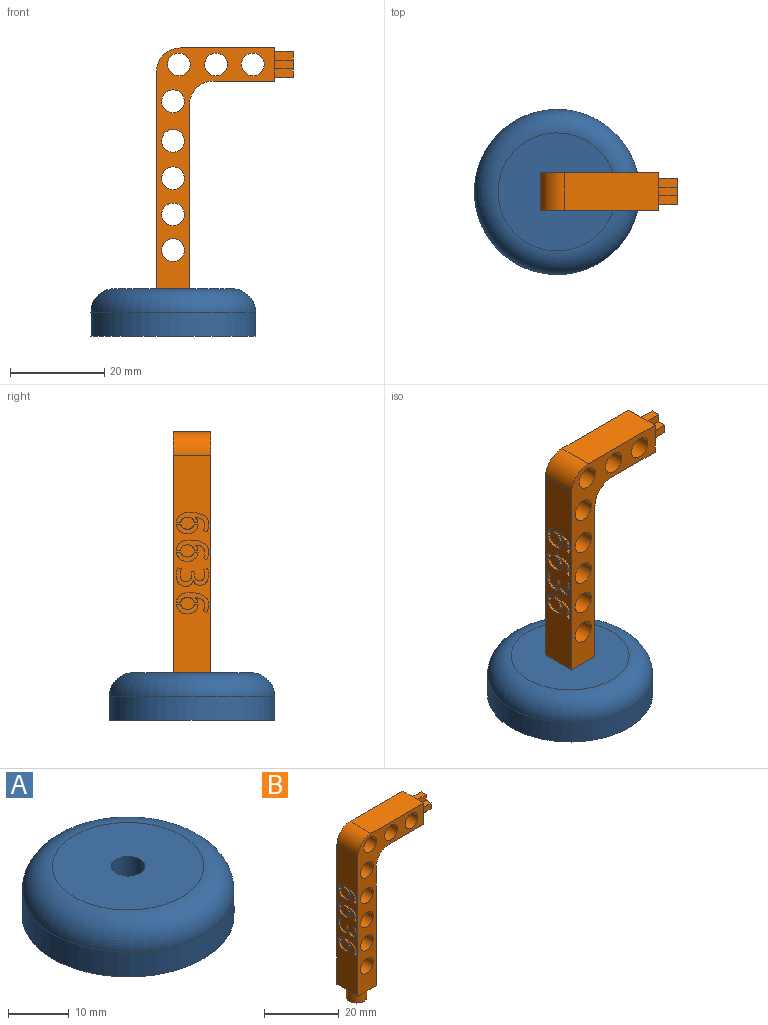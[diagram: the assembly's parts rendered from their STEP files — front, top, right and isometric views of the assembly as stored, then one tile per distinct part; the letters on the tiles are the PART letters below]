
ASSEMBLY  parts=2 mates=1
PART A: 6 faces, bbox 37.9x37.9x10 mm
  f0: cylinder r=17.5mm len=35mm, axis (0,0,-1), area 549.8mm2, adj f2,f3
  f1: plane 25x25mm, normal (0,0,1), area 466.2mm2, adj f3,f4
  f2: plane 35x35mm, normal (0,0,-1), area 962.1mm2, adj f0
  f3: torus R=12.5mm, axis (0,0,1), area 773.9mm2, adj f0,f1
  f4: cylinder r=2.8mm len=5.6mm, axis (0,0,1), area 70.4mm2, adj f1,f5
  f5: plane 5.6x5.6mm, normal (0,0,1), area 24.6mm2, adj f4
PART B: 220 faces, bbox 29x7.9x55 mm
  f0: plane 46x7.9mm, normal (-1,0,0), area 308.5mm2, adj f3,f6,f7,f8,f33,f34,f35,f36
  f1: plane 7.9x7mm, normal (1,0,0), area 38.2mm2, adj f2,f5,f6,f7,f12,f13,f14,f15
  f2: plane 20x7.9mm, normal (0,0,1), area 158mm2, adj f1,f6,f7,f8
  f3: plane 7.9x7mm, normal (0,0,-1), area 31.1mm2, adj f0,f4,f6,f7,f10
  f4: plane 39x7.9mm, normal (1,0,0), area 308.1mm2, adj f3,f6,f7,f9
  f5: plane 13x7.9mm, normal (0,0,-1), area 102.7mm2, adj f1,f6,f7,f9
  f6: plane 51x25mm, normal (0,-1,0), area 337mm2, adj f0,f1,f2,f3,f4,f5,f8,f9
  f7: plane 51x25mm, normal (0,1,0), area 337mm2, adj f0,f1,f2,f3,f4,f5,f8,f9
  f8: cylinder r=5mm len=7.9mm, axis (0,1,0), area 62mm2, adj f0,f2,f6,f7
  f9: cylinder r=5mm len=7.9mm, axis (0,-1,0), area 62mm2, adj f4,f5,f6,f7
  f10: cylinder r=2.77mm len=5.55mm, axis (0,0,1), area 69.7mm2, adj f3,f11
  f11: plane 5.55x5.55mm, normal (0,0,-1), area 24.2mm2, adj f10
  f12: plane 4x1.85mm, normal (0,0,1), area 7.4mm2, adj f1,f13,f23,f24
  f13: plane 4x1.85mm, normal (0,-1,0), area 7.4mm2, adj f1,f12,f14,f24
  f14: plane 4x1.85mm, normal (0,0,1), area 7.4mm2, adj f1,f13,f15,f24
  f15: plane 4x1.85mm, normal (0,-1,0), area 7.4mm2, adj f1,f14,f16,f24
  f16: plane 4x1.85mm, normal (0,0,-1), area 7.4mm2, adj f1,f15,f17,f24
  f17: plane 4x1.85mm, normal (0,-1,0), area 7.4mm2, adj f1,f16,f18,f24
  f18: plane 4x1.85mm, normal (0,0,-1), area 7.4mm2, adj f1,f17,f19,f24
  f19: plane 4x1.85mm, normal (0,1,0), area 7.4mm2, adj f1,f18,f20,f24
  f20: plane 4x1.85mm, normal (0,0,-1), area 7.4mm2, adj f1,f19,f21,f24
  f21: plane 4x1.85mm, normal (0,1,0), area 7.4mm2, adj f1,f20,f22,f24
  f22: plane 4x1.85mm, normal (0,0,1), area 7.4mm2, adj f1,f21,f23,f24
  f23: plane 4x1.85mm, normal (0,1,0), area 7.4mm2, adj f1,f12,f22,f24
  f24: plane 5.55x5.55mm, normal (1,0,0), area 17.1mm2, adj f12,f13,f14,f15,f16,f17,f18,f19
  f25: cylinder r=2.41mm len=7.9mm, axis (0,-1,0), area 119.6mm2, adj f6,f7
  f26: cylinder r=2.41mm len=7.9mm, axis (0,-1,0), area 119.6mm2, adj f6,f7
  f27: cylinder r=2.41mm len=7.9mm, axis (0,-1,0), area 119.6mm2, adj f6,f7
  f28: cylinder r=2.41mm len=7.9mm, axis (0,-1,0), area 119.6mm2, adj f6,f7
  f29: cylinder r=2.41mm len=7.9mm, axis (0,-1,0), area 119.6mm2, adj f6,f7
  f30: cylinder r=2.41mm len=7.9mm, axis (0,-1,0), area 119.6mm2, adj f6,f7
  f31: cylinder r=2.41mm len=7.9mm, axis (0,-1,0), area 119.6mm2, adj f6,f7
  f32: cylinder r=2.41mm len=7.9mm, axis (0,-1,0), area 119.6mm2, adj f6,f7
  f33: extruded ~0.7x0.65mm, area 0.5mm2, adj f0,f34,f63,f64
  f34: extruded ~0.72x0.7mm, area 0.5mm2, adj f0,f33,f35,f64
  f35: extruded ~0.7x0.56mm, area 0.4mm2, adj f0,f34,f36,f64
  f36: plane 0.75x0.7mm, normal (0,-0.42,0.91), area 0.6mm2, adj f0,f35,f37,f64
  f37: extruded ~0.77x0.7mm, area 0.6mm2, adj f0,f36,f38,f64
  f38: extruded ~0.96x0.7mm, area 0.7mm2, adj f0,f37,f39,f64
  f39: extruded ~0.86x0.7mm, area 0.6mm2, adj f0,f38,f40,f64
  f40: extruded ~0.78x0.7mm, area 0.7mm2, adj f0,f39,f41,f64
  f41: extruded ~1.26x0.7mm, area 1mm2, adj f0,f40,f42,f64
  f42: extruded ~2x0.7mm, area 1.4mm2, adj f0,f41,f43,f64
  f43: extruded ~1.05x0.7mm, area 0.7mm2, adj f0,f42,f44,f64
  f44: extruded ~0.84x0.7mm, area 0.7mm2, adj f0,f43,f45,f64
  f45: extruded ~0.7x0.69mm, area 0.6mm2, adj f0,f44,f46,f64
  f46: extruded ~0.97x0.7mm, area 0.7mm2, adj f0,f45,f47,f64
  f47: plane 0.89x0.7mm, normal (0,0,1), area 0.6mm2, adj f0,f46,f48,f64
  f48: extruded ~0.7x0.46mm, area 0.3mm2, adj f0,f47,f49,f64
  f49: extruded ~0.7x0.37mm, area 0.3mm2, adj f0,f48,f50,f64
  f50: extruded ~0.7x0.45mm, area 0.4mm2, adj f0,f49,f51,f64
  f51: extruded ~0.7x0.55mm, area 0.4mm2, adj f0,f50,f52,f64
  f52: extruded ~0.7x0.54mm, area 0.4mm2, adj f0,f51,f53,f64
  f53: extruded ~0.7x0.44mm, area 0.4mm2, adj f0,f52,f54,f64
  f54: extruded ~0.7x0.36mm, area 0.3mm2, adj f0,f53,f55,f64
  f55: extruded ~0.7x0.46mm, area 0.3mm2, adj f0,f54,f56,f64
  f56: plane 0.8x0.7mm, normal (0,0,1), area 0.6mm2, adj f0,f55,f57,f64
  f57: extruded ~0.7x0.66mm, area 0.5mm2, adj f0,f56,f58,f64
  f58: extruded ~0.7x0.38mm, area 0.4mm2, adj f0,f57,f59,f64
  f59: extruded ~0.7x0.04mm, area 0mm2, adj f0,f58,f60,f64
  f60: extruded ~0.7x0.04mm, area 0mm2, adj f0,f59,f61,f64
  f61: extruded ~0.74x0.7mm, area 0.5mm2, adj f0,f60,f62,f64
  f62: extruded ~0.7x0.63mm, area 0.5mm2, adj f0,f61,f63,f64
  f63: extruded ~0.7x0.45mm, area 0.4mm2, adj f0,f33,f62,f64
  f64: plane 6.8x4.15mm, normal (-1,0,0), area 9.7mm2, adj f33,f34,f35,f36,f37,f38,f39,f40
  f65: extruded ~0.7x0.43mm, area 0.3mm2, adj f0,f66,f109,f110
  f66: extruded ~0.7x0.35mm, area 0.3mm2, adj f0,f65,f67,f110
  f67: extruded ~0.7x0.35mm, area 0.3mm2, adj f0,f66,f68,f110
  f68: extruded ~0.7x0.41mm, area 0.3mm2, adj f0,f67,f69,f110
  f69: extruded ~0.7x0.51mm, area 0.4mm2, adj f0,f68,f70,f110
  f70: extruded ~0.84x0.7mm, area 0.6mm2, adj f0,f69,f71,f110
  f71: extruded ~0.7x0.58mm, area 0.5mm2, adj f0,f70,f72,f110
  f72: extruded ~0.7x0.67mm, area 0.5mm2, adj f0,f71,f73,f110
  f73: extruded ~0.81x0.7mm, area 0.6mm2, adj f0,f72,f74,f110
  f74: extruded ~0.93x0.7mm, area 0.7mm2, adj f0,f73,f75,f110
  f75: extruded ~0.7x0.54mm, area 0.4mm2, adj f0,f74,f76,f110
  f76: plane 0.82x0.7mm, normal (0,-0.36,-0.93), area 0.6mm2, adj f0,f75,f77,f110
  f77: extruded ~0.7x0.38mm, area 0.3mm2, adj f0,f76,f78,f110
  f78: extruded ~0.7x0.67mm, area 0.5mm2, adj f0,f77,f79,f110
  f79: extruded ~0.7x0.66mm, area 0.5mm2, adj f0,f78,f80,f110
  f80: extruded ~0.7x0.36mm, area 0.3mm2, adj f0,f79,f81,f110
  f81: extruded ~0.7x0.34mm, area 0.3mm2, adj f0,f80,f82,f110
  f82: extruded ~0.7x0.35mm, area 0.2mm2, adj f0,f81,f83,f110
  f83: extruded ~0.7x0.63mm, area 0.5mm2, adj f0,f82,f84,f110
  f84: extruded ~0.7x0.31mm, area 0.3mm2, adj f0,f83,f85,f110
  f85: extruded ~0.7x0.39mm, area 0.3mm2, adj f0,f84,f86,f110
  f86: extruded ~0.7x0.4mm, area 0.3mm2, adj f0,f85,f87,f110
  f87: plane 0.7x0.62mm, normal (0,1,0), area 0.4mm2, adj f0,f86,f88,f110
  f88: plane 0.74x0.7mm, normal (0,-0.01,-1), area 0.5mm2, adj f0,f87,f89,f110
  f89: plane 0.92x0.7mm, normal (0,-1,0), area 0.6mm2, adj f0,f88,f90,f110
  f90: extruded ~0.83x0.7mm, area 0.6mm2, adj f0,f89,f91,f110
  f91: extruded ~0.83x0.7mm, area 0.6mm2, adj f0,f90,f92,f110
  f92: extruded ~0.86x0.7mm, area 0.7mm2, adj f0,f91,f93,f110
  f93: extruded ~0.94x0.7mm, area 0.7mm2, adj f0,f92,f94,f110
  f94: extruded ~0.7x0.67mm, area 0.5mm2, adj f0,f93,f95,f110
  f95: extruded ~0.7x0.38mm, area 0.3mm2, adj f0,f94,f96,f110
  f96: extruded ~0.7x0.21mm, area 0.2mm2, adj f0,f95,f97,f110
  f97: extruded ~0.7x0.16mm, area 0.1mm2, adj f0,f96,f98,f110
  f98: plane 0.78x0.7mm, normal (0,0.3,-0.95), area 0.6mm2, adj f0,f97,f99,f110
  f99: extruded ~0.7x0.61mm, area 0.5mm2, adj f0,f98,f100,f110
  f100: extruded ~1.2x0.7mm, area 0.8mm2, adj f0,f99,f101,f110
  f101: extruded ~0.7x0.3mm, area 0.2mm2, adj f0,f100,f102,f110
  f102: extruded ~0.7x0.43mm, area 0.3mm2, adj f0,f101,f103,f110
  f103: extruded ~0.7x0.49mm, area 0.4mm2, adj f0,f102,f104,f110
  f104: extruded ~0.7x0.45mm, area 0.4mm2, adj f0,f103,f105,f110
  f105: extruded ~0.7x0.55mm, area 0.5mm2, adj f0,f104,f106,f110
  f106: extruded ~0.79x0.7mm, area 0.6mm2, adj f0,f105,f107,f110
  f107: extruded ~0.7x0.66mm, area 0.5mm2, adj f0,f106,f108,f110
  f108: extruded ~0.7x0.49mm, area 0.4mm2, adj f0,f107,f109,f110
  f109: extruded ~0.7x0.41mm, area 0.4mm2, adj f0,f65,f108,f110
  f110: plane 6.78x3.95mm, normal (-1,0,0), area 11.1mm2, adj f65,f66,f67,f68,f69,f70,f71,f72
  f111: extruded ~0.83x0.7mm, area 0.6mm2, adj f0,f112,f124,f125
  f112: plane 0.83x0.7mm, normal (0,0,-1), area 0.6mm2, adj f0,f111,f113,f125
  f113: extruded ~0.75x0.7mm, area 0.6mm2, adj f0,f112,f114,f125
  f114: extruded ~0.94x0.7mm, area 0.7mm2, adj f0,f113,f115,f125
  f115: extruded ~0.97x0.7mm, area 0.7mm2, adj f0,f114,f116,f125
  f116: extruded ~0.75x0.7mm, area 0.6mm2, adj f0,f115,f117,f125
  f117: plane 0.89x0.7mm, normal (0,0,-1), area 0.6mm2, adj f0,f116,f118,f125
  f118: extruded ~0.7x0.67mm, area 0.5mm2, adj f0,f117,f119,f125
  f119: extruded ~0.7x0.65mm, area 0.5mm2, adj f0,f118,f120,f125
  f120: extruded ~0.73x0.7mm, area 0.6mm2, adj f0,f119,f121,f125
  f121: extruded ~1.1x0.7mm, area 0.8mm2, adj f0,f120,f122,f125
  f122: extruded ~0.75x0.7mm, area 0.5mm2, adj f0,f121,f123,f125
  f123: extruded ~0.7x0.68mm, area 0.6mm2, adj f0,f122,f124,f125
  f124: extruded ~0.7x0.64mm, area 0.6mm2, adj f0,f111,f123,f125
  f125: plane 4.58x2mm, normal (-1,0,0), area 4.9mm2, adj f111,f112,f113,f114,f115,f116,f117,f118
  f126: extruded ~0.7x0.65mm, area 0.5mm2, adj f0,f127,f156,f157
  f127: extruded ~0.72x0.7mm, area 0.5mm2, adj f0,f126,f128,f157
  f128: extruded ~0.7x0.56mm, area 0.4mm2, adj f0,f127,f129,f157
  f129: plane 0.75x0.7mm, normal (0,-0.42,0.91), area 0.6mm2, adj f0,f128,f130,f157
  f130: extruded ~0.77x0.7mm, area 0.6mm2, adj f0,f129,f131,f157
  f131: extruded ~0.96x0.7mm, area 0.7mm2, adj f0,f130,f132,f157
  f132: extruded ~0.86x0.7mm, area 0.6mm2, adj f0,f131,f133,f157
  f133: extruded ~0.78x0.7mm, area 0.7mm2, adj f0,f132,f134,f157
  f134: extruded ~1.26x0.7mm, area 1mm2, adj f0,f133,f135,f157
  f135: extruded ~2x0.7mm, area 1.4mm2, adj f0,f134,f136,f157
  f136: extruded ~1.05x0.7mm, area 0.7mm2, adj f0,f135,f137,f157
  f137: extruded ~0.84x0.7mm, area 0.7mm2, adj f0,f136,f138,f157
  f138: extruded ~0.7x0.69mm, area 0.6mm2, adj f0,f137,f139,f157
  f139: extruded ~0.97x0.7mm, area 0.7mm2, adj f0,f138,f140,f157
  f140: plane 0.89x0.7mm, normal (0,0,1), area 0.6mm2, adj f0,f139,f141,f157
  f141: extruded ~0.7x0.46mm, area 0.3mm2, adj f0,f140,f142,f157
  f142: extruded ~0.7x0.37mm, area 0.3mm2, adj f0,f141,f143,f157
  f143: extruded ~0.7x0.45mm, area 0.4mm2, adj f0,f142,f144,f157
  f144: extruded ~0.7x0.55mm, area 0.4mm2, adj f0,f143,f145,f157
  f145: extruded ~0.7x0.54mm, area 0.4mm2, adj f0,f144,f146,f157
  f146: extruded ~0.7x0.44mm, area 0.4mm2, adj f0,f145,f147,f157
  f147: extruded ~0.7x0.36mm, area 0.3mm2, adj f0,f146,f148,f157
  f148: extruded ~0.7x0.46mm, area 0.3mm2, adj f0,f147,f149,f157
  f149: plane 0.8x0.7mm, normal (0,0,1), area 0.6mm2, adj f0,f148,f150,f157
  f150: extruded ~0.7x0.66mm, area 0.5mm2, adj f0,f149,f151,f157
  f151: extruded ~0.7x0.38mm, area 0.4mm2, adj f0,f150,f152,f157
  f152: extruded ~0.7x0.04mm, area 0mm2, adj f0,f151,f153,f157
  f153: extruded ~0.7x0.04mm, area 0mm2, adj f0,f152,f154,f157
  f154: extruded ~0.74x0.7mm, area 0.5mm2, adj f0,f153,f155,f157
  f155: extruded ~0.7x0.63mm, area 0.5mm2, adj f0,f154,f156,f157
  f156: extruded ~0.7x0.45mm, area 0.4mm2, adj f0,f126,f155,f157
  f157: plane 6.8x4.15mm, normal (-1,0,0), area 9.7mm2, adj f126,f127,f128,f129,f130,f131,f132,f133
  f158: extruded ~0.83x0.7mm, area 0.6mm2, adj f0,f159,f171,f172
  f159: plane 0.83x0.7mm, normal (0,0,-1), area 0.6mm2, adj f0,f158,f160,f172
  f160: extruded ~0.75x0.7mm, area 0.6mm2, adj f0,f159,f161,f172
  f161: extruded ~0.94x0.7mm, area 0.7mm2, adj f0,f160,f162,f172
  f162: extruded ~0.97x0.7mm, area 0.7mm2, adj f0,f161,f163,f172
  f163: extruded ~0.75x0.7mm, area 0.6mm2, adj f0,f162,f164,f172
  f164: plane 0.89x0.7mm, normal (0,0,-1), area 0.6mm2, adj f0,f163,f165,f172
  f165: extruded ~0.7x0.67mm, area 0.5mm2, adj f0,f164,f166,f172
  f166: extruded ~0.7x0.65mm, area 0.5mm2, adj f0,f165,f167,f172
  f167: extruded ~0.73x0.7mm, area 0.6mm2, adj f0,f166,f168,f172
  f168: extruded ~1.1x0.7mm, area 0.8mm2, adj f0,f167,f169,f172
  f169: extruded ~0.75x0.7mm, area 0.5mm2, adj f0,f168,f170,f172
  f170: extruded ~0.7x0.68mm, area 0.6mm2, adj f0,f169,f171,f172
  f171: extruded ~0.7x0.64mm, area 0.6mm2, adj f0,f158,f170,f172
  f172: plane 4.58x2mm, normal (-1,0,0), area 4.9mm2, adj f158,f159,f160,f161,f162,f163,f164,f165
  f173: extruded ~0.83x0.7mm, area 0.6mm2, adj f0,f174,f186,f187
  f174: plane 0.83x0.7mm, normal (0,0,-1), area 0.6mm2, adj f0,f173,f175,f187
  f175: extruded ~0.75x0.7mm, area 0.6mm2, adj f0,f174,f176,f187
  f176: extruded ~0.94x0.7mm, area 0.7mm2, adj f0,f175,f177,f187
  f177: extruded ~0.97x0.7mm, area 0.7mm2, adj f0,f176,f178,f187
  f178: extruded ~0.75x0.7mm, area 0.6mm2, adj f0,f177,f179,f187
  f179: plane 0.89x0.7mm, normal (0,0,-1), area 0.6mm2, adj f0,f178,f180,f187
  f180: extruded ~0.7x0.67mm, area 0.5mm2, adj f0,f179,f181,f187
  f181: extruded ~0.7x0.65mm, area 0.5mm2, adj f0,f180,f182,f187
  f182: extruded ~0.73x0.7mm, area 0.6mm2, adj f0,f181,f183,f187
  f183: extruded ~1.1x0.7mm, area 0.8mm2, adj f0,f182,f184,f187
  f184: extruded ~0.75x0.7mm, area 0.5mm2, adj f0,f183,f185,f187
  f185: extruded ~0.7x0.68mm, area 0.6mm2, adj f0,f184,f186,f187
  f186: extruded ~0.7x0.64mm, area 0.6mm2, adj f0,f173,f185,f187
  f187: plane 4.58x2mm, normal (-1,0,0), area 4.9mm2, adj f173,f174,f175,f176,f177,f178,f179,f180
  f188: extruded ~0.7x0.65mm, area 0.5mm2, adj f0,f189,f218,f219
  f189: extruded ~0.72x0.7mm, area 0.5mm2, adj f0,f188,f190,f219
  f190: extruded ~0.7x0.56mm, area 0.4mm2, adj f0,f189,f191,f219
  f191: plane 0.75x0.7mm, normal (0,-0.42,0.91), area 0.6mm2, adj f0,f190,f192,f219
  f192: extruded ~0.77x0.7mm, area 0.6mm2, adj f0,f191,f193,f219
  f193: extruded ~0.96x0.7mm, area 0.7mm2, adj f0,f192,f194,f219
  f194: extruded ~0.86x0.7mm, area 0.6mm2, adj f0,f193,f195,f219
  f195: extruded ~0.78x0.7mm, area 0.7mm2, adj f0,f194,f196,f219
  f196: extruded ~1.26x0.7mm, area 1mm2, adj f0,f195,f197,f219
  f197: extruded ~2x0.7mm, area 1.4mm2, adj f0,f196,f198,f219
  f198: extruded ~1.05x0.7mm, area 0.7mm2, adj f0,f197,f199,f219
  f199: extruded ~0.84x0.7mm, area 0.7mm2, adj f0,f198,f200,f219
  f200: extruded ~0.7x0.69mm, area 0.6mm2, adj f0,f199,f201,f219
  f201: extruded ~0.97x0.7mm, area 0.7mm2, adj f0,f200,f202,f219
  f202: plane 0.89x0.7mm, normal (0,0,1), area 0.6mm2, adj f0,f201,f203,f219
  f203: extruded ~0.7x0.46mm, area 0.3mm2, adj f0,f202,f204,f219
  f204: extruded ~0.7x0.37mm, area 0.3mm2, adj f0,f203,f205,f219
  f205: extruded ~0.7x0.45mm, area 0.4mm2, adj f0,f204,f206,f219
  f206: extruded ~0.7x0.55mm, area 0.4mm2, adj f0,f205,f207,f219
  f207: extruded ~0.7x0.54mm, area 0.4mm2, adj f0,f206,f208,f219
  f208: extruded ~0.7x0.44mm, area 0.4mm2, adj f0,f207,f209,f219
  f209: extruded ~0.7x0.36mm, area 0.3mm2, adj f0,f208,f210,f219
  f210: extruded ~0.7x0.46mm, area 0.3mm2, adj f0,f209,f211,f219
  f211: plane 0.8x0.7mm, normal (0,0,1), area 0.6mm2, adj f0,f210,f212,f219
  f212: extruded ~0.7x0.66mm, area 0.5mm2, adj f0,f211,f213,f219
  f213: extruded ~0.7x0.38mm, area 0.4mm2, adj f0,f212,f214,f219
  f214: extruded ~0.7x0.04mm, area 0mm2, adj f0,f213,f215,f219
  f215: extruded ~0.7x0.04mm, area 0mm2, adj f0,f214,f216,f219
  f216: extruded ~0.74x0.7mm, area 0.5mm2, adj f0,f215,f217,f219
  f217: extruded ~0.7x0.63mm, area 0.5mm2, adj f0,f216,f218,f219
  f218: extruded ~0.7x0.45mm, area 0.4mm2, adj f0,f188,f217,f219
  f219: plane 6.8x4.15mm, normal (-1,0,0), area 9.7mm2, adj f188,f189,f190,f191,f192,f193,f194,f195
PLACE A t=(-10.45,5.88,-64.84)mm
PLACE B t=(2.17,9.83,-23.51)mm
MATE fastened B.f10 <-> A.f4  axis (0,0,1) through (-10.45,5.88,-58.84)mm
